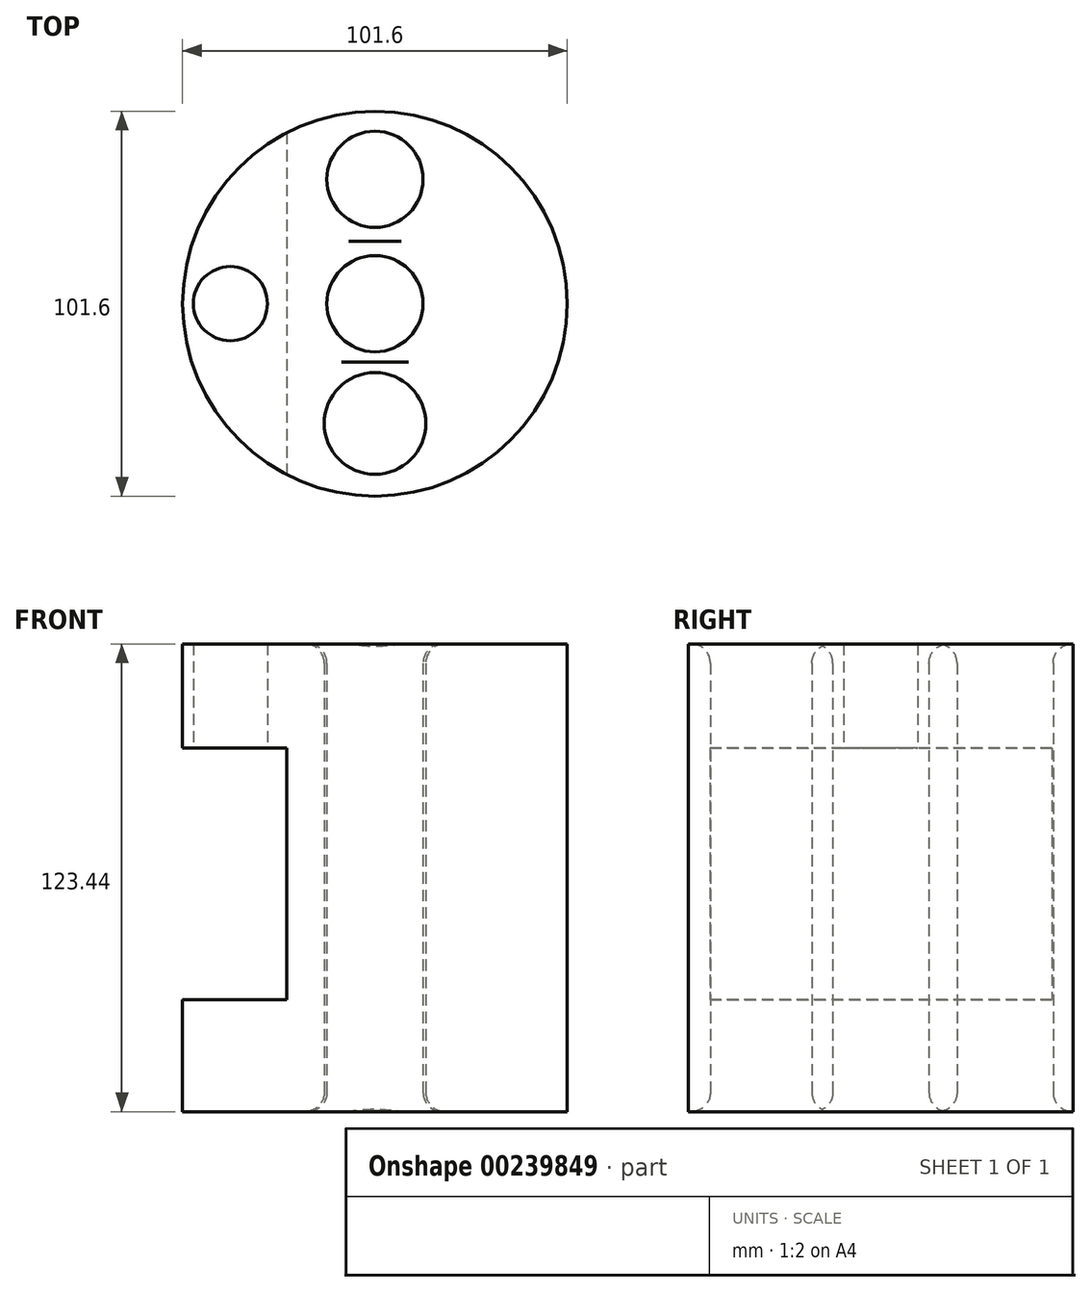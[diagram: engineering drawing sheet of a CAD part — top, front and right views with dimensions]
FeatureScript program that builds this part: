
annotation { "Feature Type Name" : "Feature", "Feature Type Description" : "" }
export const myFeature = defineFeature(function(context is Context, id is Id, definition is map)
    precondition{}
    {
        {
            var Q0;
            Q0=qCreatedBy(makeId("Top.planeOp"),FACE);
            var sketch = newSketch(context, id + "F0", { "sketchPlane" : qUnion([Q0])});
            skCircle(sketch, "E0", {"center": v(0, 0) * mm, "radius": 50.8 * mm});
            skCircle(sketch, "E1", {"center": v(0, 0) * mm, "radius": 12.7 * mm});
            skCircle(sketch, "E2", {"center": v(0, 32.8) * mm, "radius": 12.7 * mm});
            skCircle(sketch, "E3", {"center": v(0, -31.63) * mm, "radius": 13.41 * mm});
            skSolve(sketch);
        }
        {
            var Q0;
            Q0=makeQuery(id+"F0.imprint","IMPRINT",FACE,{"disambiguationData":[TD([[makeQuery(id+"F0.imprint","IMPRINT",EDGE,{"derivedFrom":sQuery(id+"F0.wireOp",EDGE,"E0")}),1.0]])]});
            extrude(context, id + "F1", {"entities" : qUnion([Q0]), "endBound" : BoundingType.SYMMETRIC, "depth" : 123.44 * mm});
        }
        {
            var Q0;
            Q0=makeQuery(id+"F1.opExtrude","SWEPT_FACE",FACE,{"disambiguationData":[OSD([sQuery(id+"F0.wireOp",EDGE,"E3")])]});
            var Q1;
            Q1=makeQuery(id+"F1.opExtrude","SWEPT_FACE",FACE,{"disambiguationData":[OSD([sQuery(id+"F0.wireOp",EDGE,"E1")])]});
            var Q2;
            Q2=makeQuery(id+"F1.opExtrude","SWEPT_FACE",FACE,{"disambiguationData":[OSD([sQuery(id+"F0.wireOp",EDGE,"E2")])]});
            fillet(context, id + "F2", {"entities" : qUnion([Q0, Q1, Q2]), "radius" : 5.08 * mm, "tangentPropagation" : true, "allowEdgeOverflow" : false});
        }
        {
            var Q0;
            Q0=qCreatedBy(makeId("Front.planeOp"),FACE);
            var sketch = newSketch(context, id + "F3", { "sketchPlane" : qUnion([Q0])});
            skLineSegment(sketch, "E4.bottom", {"start": v(-86.28, 34.25) * mm, "end": v(-23.32, 34.25) * mm});
            skLineSegment(sketch, "E4.top", {"start": v(-86.28, -32.2) * mm, "end": v(-23.32, -32.2) * mm});
            skLineSegment(sketch, "E4.left", {"start": v(-86.28, 34.25) * mm, "end": v(-86.28, -32.2) * mm});
            skLineSegment(sketch, "E4.right", {"start": v(-23.32, 34.25) * mm, "end": v(-23.32, -32.2) * mm});
            skSolve(sketch);
        }
        {
            var Q0;
            Q0 = qSketchRegion(id + "F3", true);
            extrude(context, id + "F4", {"entities" : qUnion([Q0]), "operationType" : NewBodyOperationType.REMOVE, "endBound" : BoundingType.SYMMETRIC, "oppositeDirection" : true, "depth" : 187.96 * mm});
        }
        {
            var Q0;
            Q0=qCreatedBy(makeId("Top.planeOp"),FACE);
            var sketch = newSketch(context, id + "F5", { "sketchPlane" : qUnion([Q0])});
            skCircle(sketch, "E5", {"center": v(-38.18, 0) * mm, "radius": 9.8 * mm});
            skSolve(sketch);
        }
        {
            var Q0;
            Q0 = qSketchRegion(id + "F5", true);
            extrude(context, id + "F6", {"entities" : qUnion([Q0]), "operationType" : NewBodyOperationType.REMOVE, "depth" : 90.17 * mm});
        }
    });
